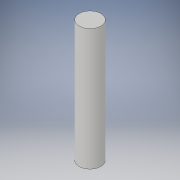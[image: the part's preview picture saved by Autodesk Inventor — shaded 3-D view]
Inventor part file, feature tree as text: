
AUTODESK INVENTOR PART (.ipt)
format: ipt  version: 2019 (Build 230136000, 136)  size: 91,136 bytes
history: native  units: mm
features: extrude x1, sketch x1
ambient origin geometry x8: Origin, YZ Plane, XZ Plane, XY Plane, X Axis, Y Axis, Z Axis, Center Point
bodies: Solid1 (feature_tree)
feature tree (2):
  extrude  "Extrusion1"  Depth=28.0mm TaperAngle=0.0deg
  sketch  "Sketch1"  dims[d0=5.0mm d1=28.0mm d2=0.0mm]
